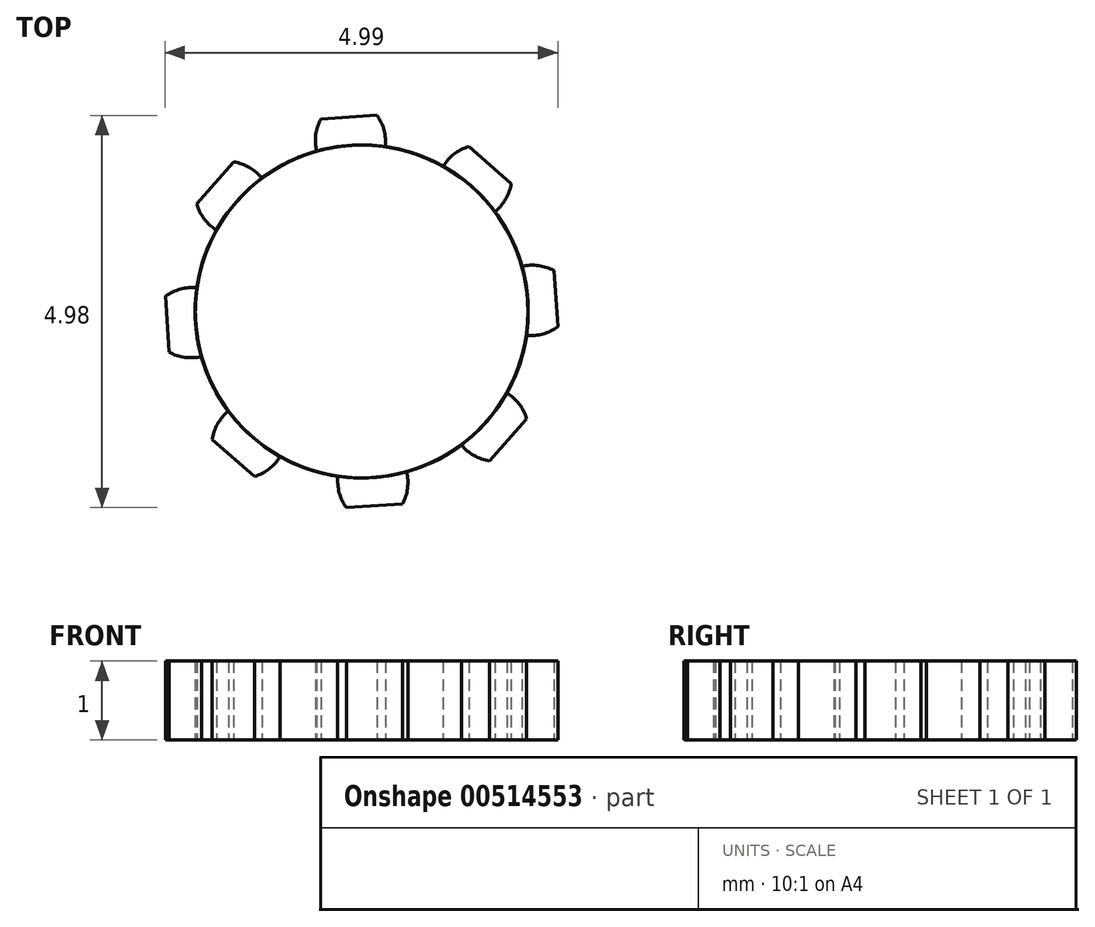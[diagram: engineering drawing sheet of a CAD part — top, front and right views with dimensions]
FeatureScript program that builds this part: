
annotation { "Feature Type Name" : "Feature", "Feature Type Description" : "" }
export const myFeature = defineFeature(function(context is Context, id is Id, definition is map)
    precondition{}
    {
        {
            var Q0;
            Q0=qCreatedBy(makeId("Top.planeOp"),FACE);
            var sketch = newSketch(context, id + "F0", { "sketchPlane" : qUnion([Q0])});
            skCircle(sketch, "E0", {"center": v(-6.84, 1.37) * mm, "radius": 2.12 * mm});
            skCircle(sketch, "E1", {"center": v(-6.84, 1.37) * mm, "radius": 2.31 * mm, "construction": true});
            skCircle(sketch, "E2", {"center": v(-6.84, 1.37) * mm, "radius": 2.5 * mm, "construction": true});
            skLineSegment(sketch, "E3", {"start": v(-6.84, 1.37) * mm, "end": v(-6.84, 4.9) * mm, "construction": true});
            skLineSegment(sketch, "E4", {"start": v(-6.84, 1.37) * mm, "end": v(-7.08, 4.96) * mm, "construction": true});
            skLineSegment(sketch, "E5", {"start": v(-6.84, 3.68) * mm, "end": v(-9.36, 3.68) * mm, "construction": true});
            skCircle(sketch, "E6", {"center": v(-6.84, 3.68) * mm, "radius": 0.57 * mm, "construction": true});
            skCircle(sketch, "E7", {"center": v(-6.84, 1.37) * mm, "radius": 2.17 * mm, "construction": true});
            skLineSegment(sketch, "E8", {"start": v(-6.84, 3.68) * mm, "end": v(-9.48, 2.16) * mm, "construction": true});
            skCircle(sketch, "E9", {"center": v(-7.11, 3.53) * mm, "radius": 0.57 * mm, "construction": true});
            skArc(sketch, "E10", {"start": v(-6.54, 3.47) * mm, "mid": v(-6.54, 3.57) * mm, "end": v(-6.56, 3.66) * mm});
            skArc(sketch, "E11", {"start": v(-6.56, 3.66) * mm, "mid": v(-6.6, 3.77) * mm, "end": v(-6.65, 3.86) * mm});
            skArc(sketch, "E12.MirrorCS", {"start": v(-7.43, 3.6) * mm, "mid": v(-7.4, 3.72) * mm, "end": v(-7.36, 3.82) * mm});
            skArc(sketch, "E13.MirrorCS", {"start": v(-7.41, 3.4) * mm, "mid": v(-7.43, 3.5) * mm, "end": v(-7.43, 3.6) * mm});
            skLineSegment(sketch, "E14", {"start": v(-7.36, 3.82) * mm, "end": v(-6.65, 3.86) * mm});
            skSolve(sketch);
        }
        {
            var Q0;
            Q0=qSketchRegion(id+"F0",true);
            extrude(context, id + "F1", {"entities" : qUnion([Q0]), "depth" : 1 * mm, "offsetDistance" : 25 * mm});
        }
        {
            var Q0;
            Q0=makeQuery(id+"F1.opExtrude","SWEPT_BODY",BODY,{"disambiguationData":[OSD([sQuery(id+"F0.wireOp",EDGE,"E0"),sQuery(id+"F0.wireOp",EDGE,"Jhyjqhsr-NoUy-XWbs-L9aD-KgkOUVdsn7Hz"),sQuery(id+"F0.wireOp",EDGE,"spiFLJTx-MjSp-7Efe-BMdC-xAXXwaFEX4Ny"),sQuery(id+"F0.wireOp",EDGE,"80abd4d4-af93-4e71-b83d-3df5c836799f0.MirrorCS"),sQuery(id+"F0.wireOp",EDGE,"ee0a7139-7228-46c4-885c-cf09280b756f0.MirrorCS"),sQuery(id+"F0.wireOp",EDGE,"TGffkZ7D-Qoxi-yTw0-Qq3I-LP4V7gg6Q0G1")])]});
            var Q1;
            Q1=makeQuery(id+"F1.opExtrude","SWEPT_FACE",FACE,{"disambiguationData":[OSD([sQuery(id+"F0.wireOp",EDGE,"E0")])]});
            circularPattern(context, id + "F2", {"entities" : qUnion([Q0]), "axis" : qUnion([Q1]), "angle" : 360 * degree, "instanceCount" : 8, "equalSpace" : true});
        }
        {
            var Q0;
            Q0 = qSketchRegion(id + "F0", true);
            extrude(context, id + "F3", {"entities" : qUnion([Q0]), "depth" : 1 * mm, "offsetDistance" : 25 * mm});
        }
    });
